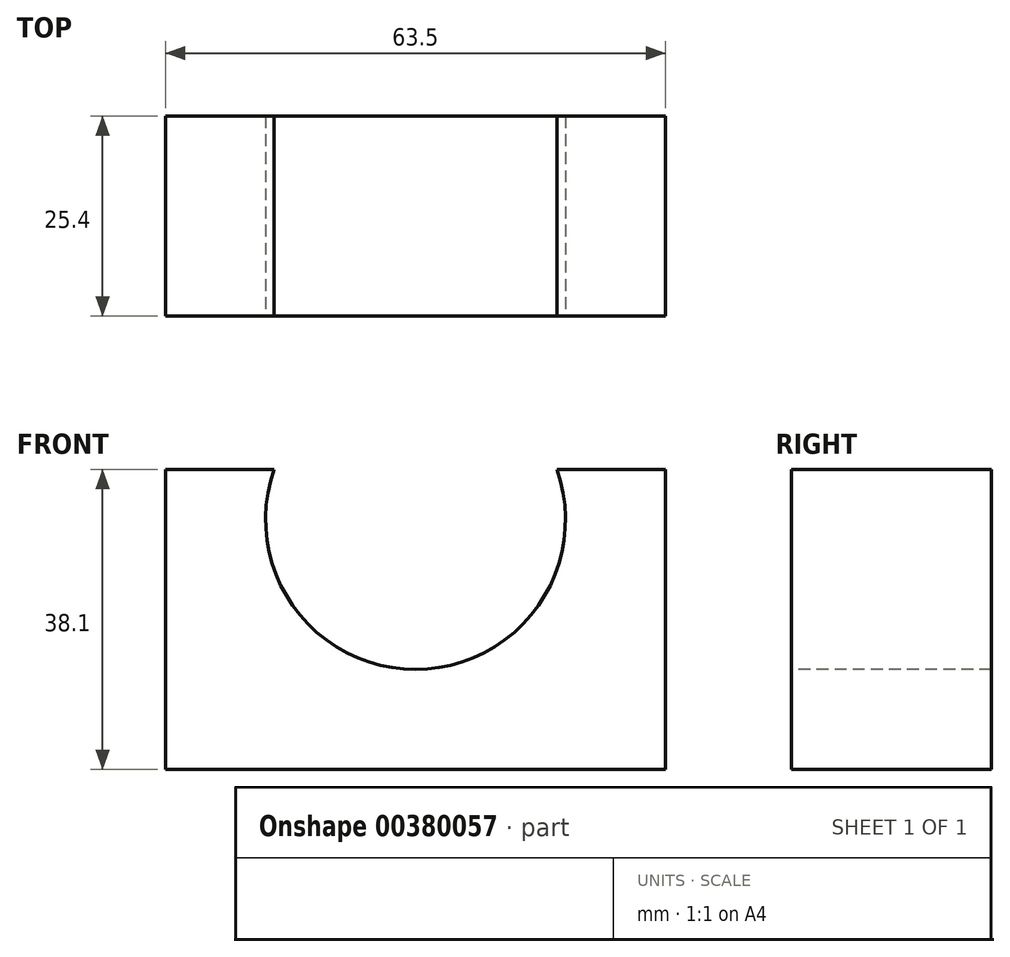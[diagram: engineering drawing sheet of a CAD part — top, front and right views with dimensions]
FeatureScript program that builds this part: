
annotation { "Feature Type Name" : "Feature", "Feature Type Description" : "" }
export const myFeature = defineFeature(function(context is Context, id is Id, definition is map)
    precondition{}
    {
        {
            var Q0;
            Q0=qCreatedBy(makeId("Front.planeOp"),FACE);
            var sketch = newSketch(context, id + "F0", { "sketchPlane" : qUnion([Q0])});
            skLineSegment(sketch, "E0", {"start": v(0, 0) * mm, "end": v(0, 38.1) * mm});
            skLineSegment(sketch, "E1", {"start": v(0, 38.1) * mm, "end": v(63.5, 38.1) * mm});
            skLineSegment(sketch, "E2", {"start": v(63.5, 38.1) * mm, "end": v(63.5, 0) * mm});
            skLineSegment(sketch, "E3", {"start": v(63.5, 0) * mm, "end": v(0, 0) * mm});
            skSolve(sketch);
        }
        {
            var Q0;
            Q0=makeQuery(id+"F0.imprint","IMPRINT",FACE,{"disambiguationData":[TD([[makeQuery(id+"F0.imprint","IMPRINT",EDGE,{"derivedFrom":sQuery(id+"F0.wireOp",EDGE,"E0")}),-1.0]])]});
            extrude(context, id + "F1", {"entities" : qUnion([Q0]), "depth" : 25.4 * mm});
        }
        {
            var Q0;
            Q0=makeQuery(id+"F1.opExtrude","CAP_FACE",FACE,{"disambiguationData":[OSD([sQuery(id+"F0.wireOp",EDGE,"E0"),sQuery(id+"F0.wireOp",EDGE,"E1"),sQuery(id+"F0.wireOp",EDGE,"E2"),sQuery(id+"F0.wireOp",EDGE,"E3")])],"isStart":false});
            var sketch = newSketch(context, id + "F2", { "sketchPlane" : qUnion([Q0])});
            skCircle(sketch, "E4", {"center": v(31.75, 31.75) * mm, "radius": 19.05 * mm});
            skPoint(sketch, "E4.centerSnap0", {"position": v(31.75, 38.1) * mm});
            skSolve(sketch);
        }
        {
            var Q0;
            {var subQ0=sQuery(id+"F2.wireOp",EDGE,"E4");var subQ1=makeQuery(id+"F1.opExtrude","CAP_EDGE",EDGE,{"disambiguationData":[OSD([sQuery(id+"F0.wireOp",EDGE,"E1")])],"isStart":false});var subQ2=makeQuery(id+"F2.imprint","INTERSECT",VERTEX,{"disambiguationData":[OD(0.0)],"derivedFrom":[subQ1,subQ0]});Q0=makeQuery(id+"F2.imprint","IMPRINT",FACE,{"disambiguationData":[TD([[makeQuery(id+"F2.imprint","IMPRINT",EDGE,{"disambiguationData":[TD([[subQ2,-1.0]])],"derivedFrom":subQ0}),1.0]])]});}
            extrude(context, id + "F3", {"entities" : qUnion([Q0]), "operationType" : NewBodyOperationType.REMOVE, "oppositeDirection" : true, "depth" : 25.4 * mm});
        }
    });
